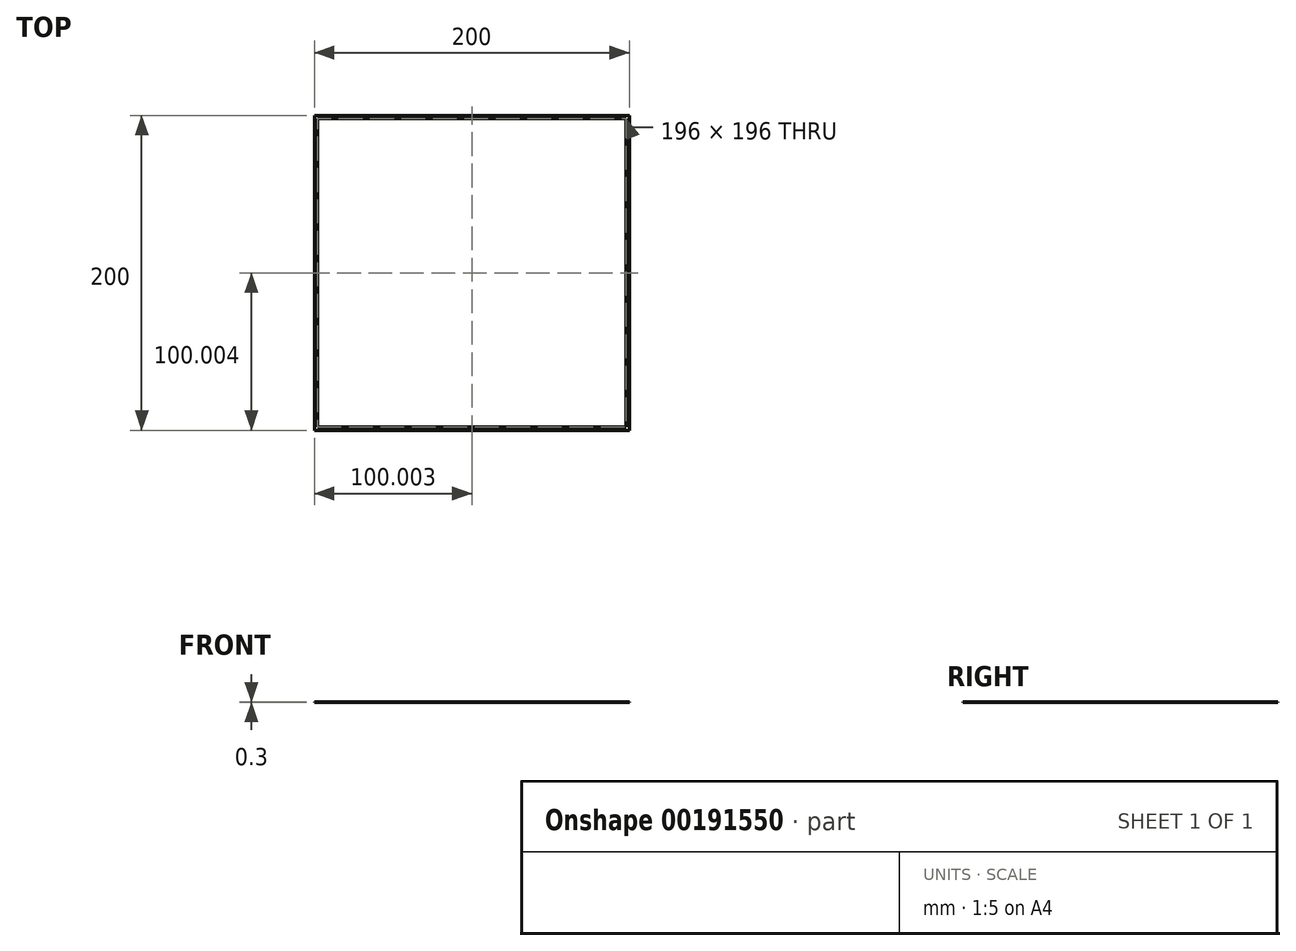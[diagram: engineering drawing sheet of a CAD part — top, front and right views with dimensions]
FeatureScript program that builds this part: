
annotation { "Feature Type Name" : "Feature", "Feature Type Description" : "" }
export const myFeature = defineFeature(function(context is Context, id is Id, definition is map)
    precondition{}
    {
        {
            var Q0;
            Q0=qCreatedBy(makeId("Top.planeOp"),FACE);
            var sketch = newSketch(context, id + "F0", { "sketchPlane" : qUnion([Q0])});
            skLineSegment(sketch, "E0.bottom", {"start": v(-128.06, -87.42) * mm, "end": v(71.94, -87.42) * mm});
            skLineSegment(sketch, "E0.top", {"start": v(-128.06, 112.58) * mm, "end": v(71.94, 112.58) * mm});
            skLineSegment(sketch, "E0.left", {"start": v(-128.06, -87.42) * mm, "end": v(-128.06, 112.58) * mm});
            skLineSegment(sketch, "E0.right", {"start": v(71.94, -87.42) * mm, "end": v(71.94, 112.58) * mm});
            skLineSegment(sketch, "E1.bottom", {"start": v(-126.06, 110.58) * mm, "end": v(69.94, 110.58) * mm});
            skLineSegment(sketch, "E1.top", {"start": v(-126.06, -85.42) * mm, "end": v(69.94, -85.42) * mm});
            skLineSegment(sketch, "E1.left", {"start": v(-126.06, 110.58) * mm, "end": v(-126.06, -85.42) * mm});
            skLineSegment(sketch, "E1.right", {"start": v(69.94, 110.58) * mm, "end": v(69.94, -85.42) * mm});
            skSolve(sketch);
        }
        {
            var Q0;
            Q0=makeQuery(id+"F0.imprint","IMPRINT",FACE,{"disambiguationData":[TD([[makeQuery(id+"F0.imprint","IMPRINT",EDGE,{"derivedFrom":sQuery(id+"F0.wireOp",EDGE,"E0.bottom")}),1.0]])]});
            extrude(context, id + "F1", {"entities" : qUnion([Q0]), "depth" : 0.3 * mm});
        }
    });
